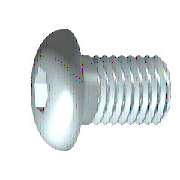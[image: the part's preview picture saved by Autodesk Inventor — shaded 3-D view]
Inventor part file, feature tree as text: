
AUTODESK INVENTOR PART (.ipt)
format: ipt  version: 2015 (Build 190159000, 159)  size: 202,240 bytes
history: native  units: mm (DEFAULTED — no unit token found)
features: sketch x2, extrude x1, plane x1, fillet x1
ambient origin geometry x7: Origin, YZ Plane, XY Plane, X Axis, Y Axis, Z Axis, Center Point
bodies: Solid1 (feature_tree), Body (feature_tree)
feature tree (5):
  extrude  "Slot"  Depth=2.5654mm
  plane  "Work Plane1"
  fillet  "Fillet2"  Radius=2.5654mm
  sketch  "Sketch1"  dims[d1=7.4166mm d2=2.1083mm d3=2.5654mm]
  sketch  "Sketch2"  dims[d4=1.778mm d5=60.0deg d6=4.826mm d7=4.826mm d8=3.666174mm d9=9.1694mm d10=90.0deg d11=10.0mm d12=0.0mm d13=7.4166mm d14=0.0mm d15=0.649224mm d16=0.649224mm d17=2.3114mm d19=0.0mm d26=9.525mm d27=45.0deg d28=0.0mm d29=0.0mm d30=0.1mm]
